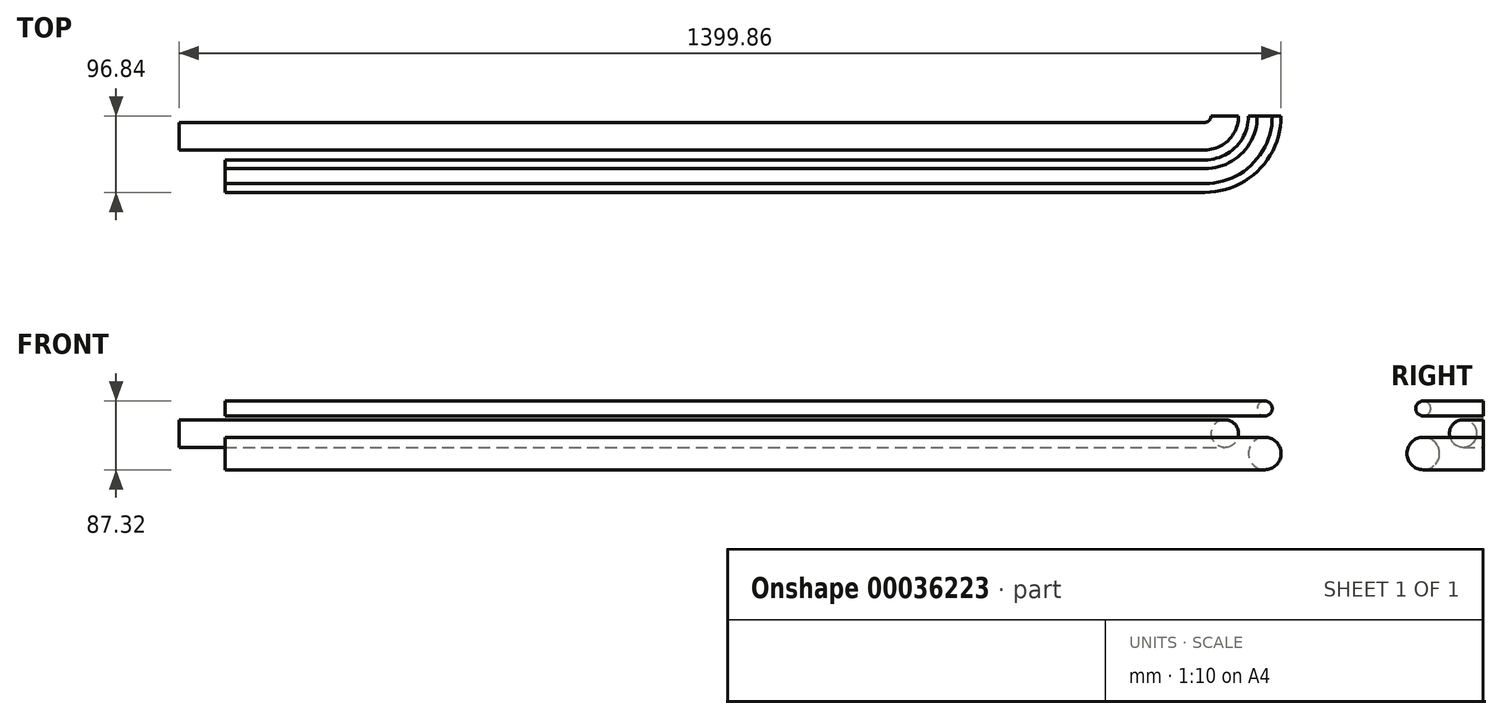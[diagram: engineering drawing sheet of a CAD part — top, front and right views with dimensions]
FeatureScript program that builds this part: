
annotation { "Feature Type Name" : "Feature", "Feature Type Description" : "" }
export const myFeature = defineFeature(function(context is Context, id is Id, definition is map)
    precondition{}
    {
        {
            var Q0;
            Q0=qCreatedBy(makeId("Right.planeOp"),FACE);
            var sketch = newSketch(context, id + "F0", { "sketchPlane" : qUnion([Q0])});
            skCircle(sketch, "E0", {"center": v(0, 0) * mm, "radius": 20.64 * mm});
            skCircle(sketch, "E1", {"center": v(0, 57.15) * mm, "radius": 9.53 * mm});
            skCircle(sketch, "E2", {"center": v(50.8, 25.4) * mm, "radius": 17.46 * mm});
            skSolve(sketch);
        }
        {
            var Q0;
            Q0=qCreatedBy(makeId("Top.planeOp"),FACE);
            var sketch = newSketch(context, id + "F1", { "sketchPlane" : qUnion([Q0])});
            skLineSegment(sketch, "E3", {"start": v(0, 0) * mm, "end": v(1244.6, 0) * mm});
            skArc(sketch, "E4", {"start": v(1244.6, 0) * mm, "mid": v(1298.48, 22.32) * mm, "end": v(1320.8, 76.2) * mm});
            skLineSegment(sketch, "E5", {"start": v(1320.8, 76.2) * mm, "end": v(1244.6, 76.2) * mm, "construction": true});
            skSolve(sketch);
        }
        {
            var Q0;
            Q0 = qSketchRegion(id + "F0", true);
            var Q1;
            Q1=sQuery(id+"F1.wireOp",EDGE,"E3");
            var Q2;
            Q2=sQuery(id+"F1.wireOp",EDGE,"E4");
            sweep(context, id + "F2", {"profiles" : qUnion([Q0]), "path" : qUnion([Q1, Q2])});
        }
        {
            var Q0;
            Q0=makeQuery(id+"F2.opSweep","CAP_FACE",FACE,{"disambiguationData":[OSD([sQuery(id+"F0.wireOp",EDGE,"E2"),sQuery(id+"F1.wireOp",VERTEX,"E3.start")])],"isStart":true});
            extrude(context, id + "F3", {"entities" : qUnion([Q0]), "operationType" : NewBodyOperationType.ADD, "depth" : 58.42 * mm});
        }
    });
